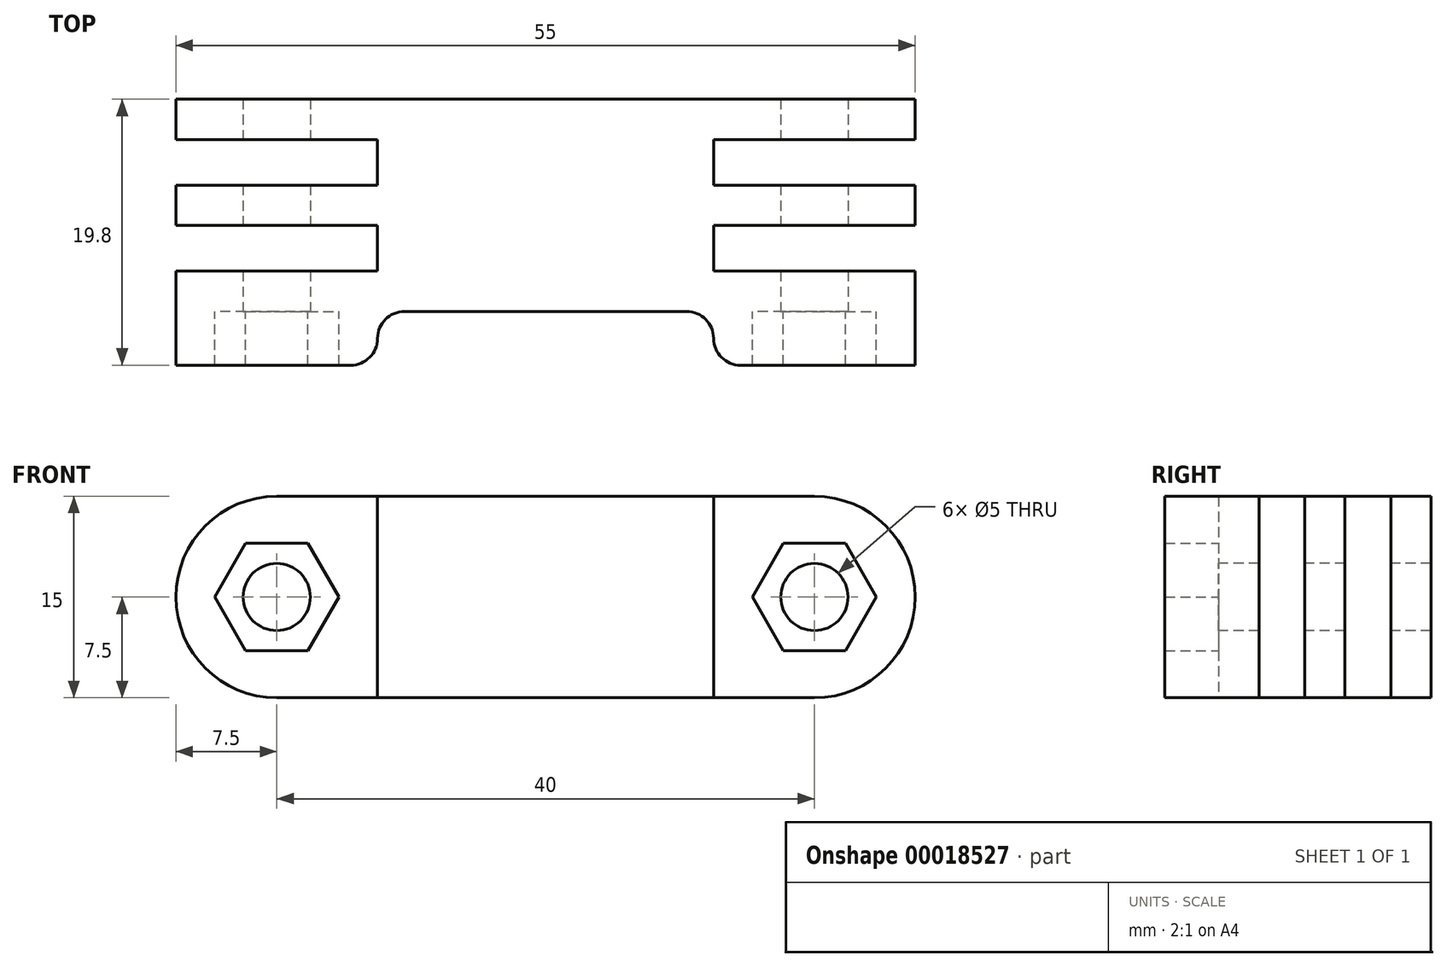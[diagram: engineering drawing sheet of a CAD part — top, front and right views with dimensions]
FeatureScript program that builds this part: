
annotation { "Feature Type Name" : "Feature", "Feature Type Description" : "" }
export const myFeature = defineFeature(function(context is Context, id is Id, definition is map)
    precondition{}
    {
        {
            var Q0;
            Q0=qCreatedBy(makeId("Front.planeOp"),FACE);
            var sketch = newSketch(context, id + "F0", { "sketchPlane" : qUnion([Q0])});
            skCircle(sketch, "E0", {"center": v(0, 0) * mm, "radius": 7.5 * mm});
            skCircle(sketch, "E1", {"center": v(0, 0) * mm, "radius": 2.5 * mm});
            skLineSegment(sketch, "E2.bottom", {"start": v(-7.5, 7.5) * mm, "end": v(7.5, 7.5) * mm});
            skLineSegment(sketch, "E2.top", {"start": v(-7.5, -7.5) * mm, "end": v(7.5, -7.5) * mm});
            skLineSegment(sketch, "E2.left", {"start": v(-7.5, 7.5) * mm, "end": v(-7.5, -7.5) * mm});
            skLineSegment(sketch, "E2.right", {"start": v(7.5, 7.5) * mm, "end": v(7.5, -7.5) * mm});
            skPoint(sketch, "E3", {"position": v(0, 7.5) * mm});
            skCircle(sketch, "E4.cCircle", {"center": v(0, 0) * mm, "radius": 4 * mm, "construction": true});
            skLineSegment(sketch, "E4.0", {"start": v(4.62, 0) * mm, "end": v(2.3, -4) * mm});
            skLineSegment(sketch, "E4.1", {"start": v(2.3, -4) * mm, "end": v(-2.3, -4) * mm});
            skLineSegment(sketch, "E4.2", {"start": v(-2.3, -4) * mm, "end": v(-4.62, 0) * mm});
            skLineSegment(sketch, "E4.3", {"start": v(-4.62, 0) * mm, "end": v(-2.3, 4) * mm});
            skLineSegment(sketch, "E4.4", {"start": v(-2.3, 4) * mm, "end": v(2.3, 4) * mm});
            skLineSegment(sketch, "E4.5", {"start": v(2.3, 4) * mm, "end": v(4.62, 0) * mm});
            skPoint(sketch, "E4.0.midPoint", {"position": v(3.46, -2) * mm});
            skSolve(sketch);
        }
        {
            var Q0;
            Q0=qCreatedBy(makeId("Right.planeOp"),FACE);
            var sketch = newSketch(context, id + "F1", { "sketchPlane" : qUnion([Q0])});
            skLineSegment(sketch, "E5.bottom", {"start": v(-7.9, 7.5) * mm, "end": v(-4.9, 7.5) * mm});
            skLineSegment(sketch, "E5.top", {"start": v(-7.9, -7.5) * mm, "end": v(-4.9, -7.5) * mm});
            skLineSegment(sketch, "E5.left", {"start": v(-7.9, 7.5) * mm, "end": v(-7.9, -7.5) * mm});
            skLineSegment(sketch, "E5.right", {"start": v(-4.9, 7.5) * mm, "end": v(-4.9, -7.5) * mm});
            skLineSegment(sketch, "E6.bottom", {"start": v(-1.5, 7.5) * mm, "end": v(1.5, 7.5) * mm});
            skLineSegment(sketch, "E6.top", {"start": v(-1.5, -7.5) * mm, "end": v(1.5, -7.5) * mm});
            skLineSegment(sketch, "E6.left", {"start": v(-1.5, 7.5) * mm, "end": v(-1.5, -7.5) * mm});
            skLineSegment(sketch, "E6.right", {"start": v(1.5, 7.5) * mm, "end": v(1.5, -7.5) * mm});
            skLineSegment(sketch, "E7.bottom", {"start": v(4.9, 7.5) * mm, "end": v(7.9, 7.5) * mm});
            skLineSegment(sketch, "E7.top", {"start": v(4.9, -7.5) * mm, "end": v(7.9, -7.5) * mm});
            skLineSegment(sketch, "E7.left", {"start": v(4.9, 7.5) * mm, "end": v(4.9, -7.5) * mm});
            skLineSegment(sketch, "E7.right", {"start": v(7.9, 7.5) * mm, "end": v(7.9, -7.5) * mm});
            skLineSegment(sketch, "E8", {"start": v(-4.9, 7.5) * mm, "end": v(-1.5, 7.5) * mm});
            skLineSegment(sketch, "E9", {"start": v(-4.9, -7.5) * mm, "end": v(-1.5, -7.5) * mm});
            skLineSegment(sketch, "E10", {"start": v(1.5, -7.5) * mm, "end": v(4.9, -7.5) * mm});
            skLineSegment(sketch, "E11", {"start": v(1.5, 7.5) * mm, "end": v(4.9, 7.5) * mm});
            skSolve(sketch);
        }
        {
            var Q0;
            Q0=makeQuery(id+"F1.imprint","IMPRINT",FACE,{"disambiguationData":[TD([[makeQuery(id+"F1.imprint","IMPRINT",EDGE,{"derivedFrom":sQuery(id+"F1.wireOp",EDGE,"E5.bottom")}),-1.0]])]});
            var Q1;
            Q1=makeQuery(id+"F1.imprint","IMPRINT",FACE,{"disambiguationData":[TD([[makeQuery(id+"F1.imprint","IMPRINT",EDGE,{"derivedFrom":sQuery(id+"F1.wireOp",EDGE,"E5.right")}),1.0]])]});
            var Q2;
            Q2=makeQuery(id+"F1.imprint","IMPRINT",FACE,{"disambiguationData":[TD([[makeQuery(id+"F1.imprint","IMPRINT",EDGE,{"derivedFrom":sQuery(id+"F1.wireOp",EDGE,"E6.bottom")}),-1.0]])]});
            var Q3;
            Q3=makeQuery(id+"F1.imprint","IMPRINT",FACE,{"disambiguationData":[TD([[makeQuery(id+"F1.imprint","IMPRINT",EDGE,{"derivedFrom":sQuery(id+"F1.wireOp",EDGE,"E6.right")}),1.0]])]});
            var Q4;
            Q4=makeQuery(id+"F1.imprint","IMPRINT",FACE,{"disambiguationData":[TD([[makeQuery(id+"F1.imprint","IMPRINT",EDGE,{"derivedFrom":sQuery(id+"F1.wireOp",EDGE,"E7.bottom")}),-1.0]])]});
            extrude(context, id + "F2", {"entities" : qUnion([Q0, Q1, Q2, Q3, Q4]), "oppositeDirection" : true, "depth" : (40 / 2) * mm});
        }
        {
            var Q0;
            {var subQ3=sQuery(id+"F0.wireOp",EDGE,"bc1313fc-6ac6-41b2-a0ec-b62939a70bd7");Q0=makeQuery(id+"F0.imprint","IMPRINT",FACE,{"disambiguationData":[TD([[makeQuery(id+"F0.imprint","IMPRINT",EDGE,{"derivedFrom":subQ3}),1.0]])]});}
            var Q1;
            {var subQ0=sQuery(id+"F0.wireOp",EDGE,"5e39aa90-c507-43f0-988f-fcf05e70d7be");Q1=makeQuery(id+"F0.imprint","IMPRINT",FACE,{"disambiguationData":[TD([[makeQuery(id+"F0.imprint","IMPRINT",EDGE,{"derivedFrom":subQ0}),1.0]])]});}
            var Q2;
            Q2=makeQuery(id+"F0.imprint","IMPRINT",FACE,{"disambiguationData":[TD([[makeQuery(id+"F0.imprint","IMPRINT",EDGE,{"derivedFrom":sQuery(id+"F0.wireOp",EDGE,"E4.0")}),1.0]])]});
            var Q3;
            Q3=makeQuery(id+"F0.imprint","IMPRINT",FACE,{"disambiguationData":[TD([[makeQuery(id+"F0.imprint","IMPRINT",EDGE,{"derivedFrom":sQuery(id+"F0.wireOp",EDGE,"E1")}),1.0]])]});
            var Q4;
            Q4=makeQuery(id+"F0.imprint","IMPRINT",FACE,{"disambiguationData":[TD([[makeQuery(id+"F0.imprint","IMPRINT",EDGE,{"derivedFrom":sQuery(id+"F0.wireOp",EDGE,"E1")}),-1.0]])]});
            var Q5;
            Q5=makeQuery(id+"F2.opExtrude","SWEPT_FACE",FACE,{"disambiguationData":[OSD([sQuery(id+"F1.wireOp",EDGE,"E5.left")])]});
            var Q6;
            Q6=makeQuery(id+"F2.opExtrude","SWEPT_FACE",FACE,{"disambiguationData":[OSD([sQuery(id+"F1.wireOp",EDGE,"E7.right")])]});
            extrude(context, id + "F3", {"entities" : qUnion([Q0, Q1, Q2, Q3, Q4]), "operationType" : NewBodyOperationType.ADD, "endBound" : BoundingType.UP_TO_SURFACE, "endBoundEntityFace" : qUnion([Q5]), "depth" : 25 * mm, "hasSecondDirection" : true, "secondDirectionBound" : SecondDirectionBoundingType.UP_TO_SURFACE, "secondDirectionOppositeDirection" : true, "secondDirectionBoundEntityFace" : qUnion([Q6]), "secondDirectionDepth" : 25 * mm});
        }
        {
            var Q0;
            Q0=makeQuery(id+"F3.boolean.opBoolean","MERGE",FACE,{"derivedFrom":[makeQuery(id+"F2.opExtrude","SWEPT_FACE",FACE,{"disambiguationData":[OSD([sQuery(id+"F1.wireOp",EDGE,"E5.left")])]}),makeQuery(id+"F3.opExtrude","CAP_FACE",FACE,{"disambiguationData":[OSD([sQuery(id+"F0.wireOp",EDGE,"E0")])],"isStart":false})]});
            var sketch = newSketch(context, id + "F4", { "sketchPlane" : qUnion([Q0])});
            skCircle(sketch, "E12.cCircle", {"center": v(0, 0) * mm, "radius": 4 * mm, "construction": true});
            skLineSegment(sketch, "E12.0", {"start": v(4.62, 0) * mm, "end": v(2.3, -4) * mm});
            skLineSegment(sketch, "E12.1", {"start": v(2.3, -4) * mm, "end": v(-2.3, -4) * mm});
            skLineSegment(sketch, "E12.2", {"start": v(-2.3, -4) * mm, "end": v(-4.62, 0) * mm});
            skLineSegment(sketch, "E12.3", {"start": v(-4.62, 0) * mm, "end": v(-2.3, 4) * mm});
            skLineSegment(sketch, "E12.4", {"start": v(-2.3, 4) * mm, "end": v(2.3, 4) * mm});
            skLineSegment(sketch, "E12.5", {"start": v(2.3, 4) * mm, "end": v(4.62, 0) * mm});
            skPoint(sketch, "E12.0.midPoint", {"position": v(3.46, -2) * mm});
            skCircle(sketch, "E13", {"center": v(0, 0) * mm, "radius": 7.5 * mm});
            skLineSegment(sketch, "E14.rect.bottom", {"start": v(7.5, 7.5) * mm, "end": v(-7.5, 7.5) * mm});
            skLineSegment(sketch, "E14.rect.top", {"start": v(7.5, -7.5) * mm, "end": v(-7.5, -7.5) * mm});
            skLineSegment(sketch, "E14.rect.left", {"start": v(7.5, 7.5) * mm, "end": v(7.5, -7.5) * mm});
            skLineSegment(sketch, "E14.rect.right", {"start": v(-7.5, 7.5) * mm, "end": v(-7.5, -7.5) * mm});
            skSolve(sketch);
        }
        {
            var Q0;
            Q0=makeQuery(id+"F4.imprint","IMPRINT",FACE,{"disambiguationData":[TD([[makeQuery(id+"F4.imprint","IMPRINT",EDGE,{"derivedFrom":sQuery(id+"F4.wireOp",EDGE,"E12.0")}),1.0]])]});
            var Q1;
            {var subQ1=sQuery(id+"F4.wireOp",EDGE,"E13");var subQ3=sQuery(id+"F4.wireOp",EDGE,"E14.rect.top");var subQ5=makeQuery(id+"F4.imprint","INTERSECT",VERTEX,{"derivedFrom":[subQ1,subQ3]});Q1=makeQuery(id+"F4.imprint","IMPRINT",FACE,{"disambiguationData":[TD([[makeQuery(id+"F4.imprint","IMPRINT",EDGE,{"disambiguationData":[TD([[subQ5,1.0]])],"derivedFrom":subQ1}),-1.0]])]});}
            var Q2;
            {var subQ1=sQuery(id+"F4.wireOp",EDGE,"E13");var subQ3=sQuery(id+"F4.wireOp",EDGE,"E14.rect.bottom");var subQ5=makeQuery(id+"F4.imprint","INTERSECT",VERTEX,{"derivedFrom":[subQ1,subQ3]});Q2=makeQuery(id+"F4.imprint","IMPRINT",FACE,{"disambiguationData":[TD([[makeQuery(id+"F4.imprint","IMPRINT",EDGE,{"disambiguationData":[TD([[subQ5,-1.0]])],"derivedFrom":subQ1}),-1.0]])]});}
            extrude(context, id + "F5", {"entities" : qUnion([Q0, Q1, Q2]), "operationType" : NewBodyOperationType.ADD, "depth" : 4 * mm});
        }
        {
            var Q0;
            Q0=makeQuery(id+"F5.opExtrude","CAP_EDGE",EDGE,{"disambiguationData":[OSD([sQuery(id+"F4.wireOp",EDGE,"E14.rect.right")])],"isStart":true});
            var Q1;
            Q1=makeQuery(id+"F5.opExtrude","CAP_EDGE",EDGE,{"disambiguationData":[OSD([sQuery(id+"F4.wireOp",EDGE,"E14.rect.right")])],"isStart":false});
            fillet(context, id + "F6", {"entities" : qUnion([Q0, Q1]), "radius" : 2 * mm, "tangentPropagation" : true, "allowEdgeOverflow" : false});
        }
        {
            var Q0;
            Q0=makeQuery(id+"F1.imprint","IMPRINT",FACE,{"disambiguationData":[TD([[makeQuery(id+"F1.imprint","IMPRINT",EDGE,{"derivedFrom":sQuery(id+"F1.wireOp",EDGE,"E5.right")}),1.0]])]});
            var Q1;
            Q1=makeQuery(id+"F1.imprint","IMPRINT",FACE,{"disambiguationData":[TD([[makeQuery(id+"F1.imprint","IMPRINT",EDGE,{"derivedFrom":sQuery(id+"F1.wireOp",EDGE,"E6.right")}),1.0]])]});
            extrude(context, id + "F7", {"entities" : qUnion([Q0, Q1]), "operationType" : NewBodyOperationType.REMOVE, "endBound" : BoundingType.SYMMETRIC, "oppositeDirection" : true, "depth" : 15 * mm});
        }
        {
            var Q0;
            Q0=makeQuery(id+"F0.imprint","IMPRINT",FACE,{"disambiguationData":[TD([[makeQuery(id+"F0.imprint","IMPRINT",EDGE,{"derivedFrom":sQuery(id+"F0.wireOp",EDGE,"E1")}),1.0]])]});
            extrude(context, id + "F8", {"entities" : qUnion([Q0]), "operationType" : NewBodyOperationType.REMOVE, "endBound" : BoundingType.THROUGH_ALL, "oppositeDirection" : true, "depth" : 25 * mm, "hasSecondDirection" : true, "secondDirectionBound" : SecondDirectionBoundingType.THROUGH_ALL, "secondDirectionOppositeDirection" : false, "secondDirectionDepth" : 25 * mm});
        }
        {
            var Q0;
            Q0=makeQuery(id+"F2.opExtrude","SWEPT_BODY",BODY,{"disambiguationData":[OSD([sQuery(id+"F1.wireOp",EDGE,"E5.bottom"),sQuery(id+"F1.wireOp",EDGE,"E5.top"),sQuery(id+"F1.wireOp",EDGE,"E5.left"),sQuery(id+"F1.wireOp",EDGE,"E6.bottom"),sQuery(id+"F1.wireOp",EDGE,"E6.top"),sQuery(id+"F1.wireOp",EDGE,"E7.bottom"),sQuery(id+"F1.wireOp",EDGE,"E7.top"),sQuery(id+"F1.wireOp",EDGE,"E7.right"),sQuery(id+"F1.wireOp",EDGE,"E8"),sQuery(id+"F1.wireOp",EDGE,"E9"),sQuery(id+"F1.wireOp",EDGE,"E10"),sQuery(id+"F1.wireOp",EDGE,"E11")])]});
            var Q1;
            Q1=makeQuery(id+"F2.opExtrude","CAP_FACE",FACE,{"disambiguationData":[OSD([sQuery(id+"F1.wireOp",EDGE,"E5.bottom"),sQuery(id+"F1.wireOp",EDGE,"E5.top"),sQuery(id+"F1.wireOp",EDGE,"E5.left"),sQuery(id+"F1.wireOp",EDGE,"E6.bottom"),sQuery(id+"F1.wireOp",EDGE,"E6.top"),sQuery(id+"F1.wireOp",EDGE,"E7.bottom"),sQuery(id+"F1.wireOp",EDGE,"E7.top"),sQuery(id+"F1.wireOp",EDGE,"E7.right"),sQuery(id+"F1.wireOp",EDGE,"E8"),sQuery(id+"F1.wireOp",EDGE,"E9"),sQuery(id+"F1.wireOp",EDGE,"E10"),sQuery(id+"F1.wireOp",EDGE,"E11")])],"isStart":false});
            mirror(context, id + "F9", {"operationType" : NewBodyOperationType.ADD, "entities" : qUnion([Q0]), "mirrorPlane" : qUnion([Q1])});
        }
    });
